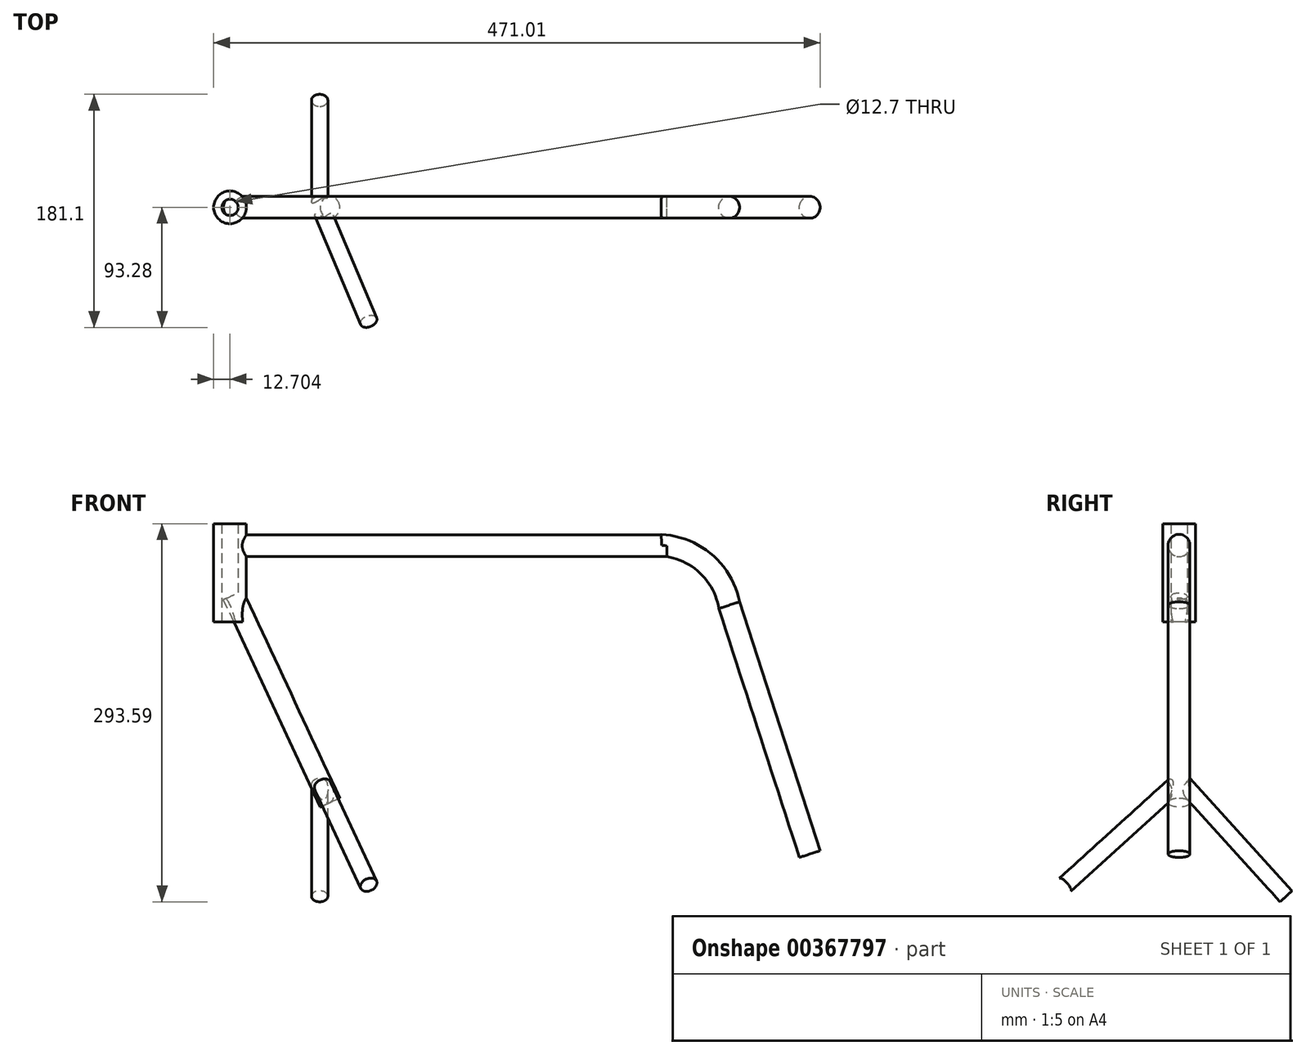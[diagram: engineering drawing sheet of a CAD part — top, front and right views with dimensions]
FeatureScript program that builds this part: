
annotation { "Feature Type Name" : "Feature", "Feature Type Description" : "" }
export const myFeature = defineFeature(function(context is Context, id is Id, definition is map)
    precondition{}
    {
        {
            var Q0;
            Q0=qCreatedBy(makeId("Top.planeOp"),FACE);
            var sketch = newSketch(context, id + "F0", { "sketchPlane" : qUnion([Q0])});
            skCircle(sketch, "E0", {"center": v(-127.53, 0) * mm, "radius": 12.7 * mm});
            skSolve(sketch);
        }
        {
            var Q0;
            Q0 = qSketchRegion(id + "F0", true);
            extrude(context, id + "F1", {"entities" : qUnion([Q0]), "depth" : 76.2 * mm});
        }
        {
            var Q0;
            Q0=makeQuery(id+"F1.opExtrude","CAP_FACE",FACE,{"disambiguationData":[OSD([sQuery(id+"F0.wireOp",EDGE,"E0")])],"isStart":false});
            var sketch = newSketch(context, id + "F2", { "sketchPlane" : qUnion([Q0])});
            skPoint(sketch, "E1", {"position": v(-127.53, 0) * mm});
            skSolve(sketch);
        }
        {
            var Q0;
            Q0=makeQuery(id+"F1.opExtrude","CAP_FACE",FACE,{"disambiguationData":[OSD([sQuery(id+"F0.wireOp",EDGE,"E0")])],"isStart":true});
            var sketch = newSketch(context, id + "F3", { "sketchPlane" : qUnion([Q0])});
            skPoint(sketch, "E2", {"position": v(-127.53, 0) * mm});
            skSolve(sketch);
        }
        {
            var Q0;
            Q0=sQuery(id+"F3.wireOp",VERTEX,"E2");
            var Q1;
            Q1=sQuery(id+"F2.wireOp",VERTEX,"E1");
            var Q2;
            Q2=makeQuery(id+"F1.opExtrude","SWEPT_BODY",BODY,{"disambiguationData":[OSD([sQuery(id+"F0.wireOp",EDGE,"E0")])]});
            hole(context, id + "F4", {"style" : HoleStyle.SIMPLE, "endStyle" : HoleEndStyle.THROUGH, "holeDiameter" : 12.7 * mm, "isTappedThrough" : true, "tappedDepth" : 12.7 * mm, "tapClearance" : 3, "locations" : qUnion([Q0, Q1]), "scope" : qUnion([Q2])});
        }
        {
            var Q0;
            Q0=qCreatedBy(makeId("Right.planeOp"),FACE);
            cPlane(context, id + "F5", {"entities" : qUnion([Q0]), "cplaneType" : CPlaneType.OFFSET, "offset" : 118.49 * mm, "oppositeDirection" : true, "width" : 152.4 * mm, "height" : 152.4 * mm});
        }
        {
            var Q0;
            Q0=qCreatedBy(id+"F5.planeOp",FACE);
            var sketch = newSketch(context, id + "F6", { "sketchPlane" : qUnion([Q0])});
            skCircle(sketch, "E3", {"center": v(0, 59.12) * mm, "radius": 8.47 * mm});
            skSolve(sketch);
        }
        {
            var Q0;
            Q0 = qSketchRegion(id + "F6", true);
            extrude(context, id + "F7", {"entities" : qUnion([Q0]), "operationType" : NewBodyOperationType.ADD, "depth" : 330.2 * mm});
        }
        {
            var Q0;
            Q0=qCreatedBy(id+"F5.planeOp",FACE);
            var sketch = newSketch(context, id + "F8", { "sketchPlane" : qUnion([Q0])});
            skLineSegment(sketch, "E4", {"start": v(0, 23.85) * mm, "end": v(152.27, 23.85) * mm});
            skSolve(sketch);
        }
        {
            var Q0;
            Q0=qCreatedBy(id+"F5.planeOp",FACE);
            var Q1;
            Q1=sQuery(id+"F8.wireOp",EDGE,"E4");
            cPlane(context, id + "F9", {"entities" : qUnion([Q0, Q1]), "cplaneType" : CPlaneType.LINE_ANGLE, "offset" : 25.4 * mm, "angle" : 65 * degree, "width" : 152.4 * mm, "height" : 152.4 * mm});
        }
        {
            var Q0;
            Q0=qCreatedBy(id+"F9.planeOp",FACE);
            var sketch = newSketch(context, id + "F10", { "sketchPlane" : qUnion([Q0])});
            skCircle(sketch, "E5", {"center": v(-104.52, 0) * mm, "radius": 8.38 * mm});
            skSolve(sketch);
        }
        {
            var Q0;
            Q0 = qSketchRegion(id + "F10", true);
            extrude(context, id + "F11", {"entities" : qUnion([Q0]), "operationType" : NewBodyOperationType.ADD, "oppositeDirection" : true, "depth" : 177.8 * mm});
        }
        {
            var Q0;
            Q0=qCreatedBy(id+"F9.planeOp",FACE);
            cPlane(context, id + "F12", {"entities" : qUnion([Q0]), "cplaneType" : CPlaneType.OFFSET, "offset" : 166.54 * mm, "oppositeDirection" : true, "width" : 152.4 * mm, "height" : 152.4 * mm});
        }
        {
            var Q0;
            Q0=qCreatedBy(id+"F12.planeOp",FACE);
            var sketch = newSketch(context, id + "F13", { "sketchPlane" : qUnion([Q0])});
            skLineSegment(sketch, "E6", {"start": v(0, 72.18) * mm, "end": v(-141.83, 72.18) * mm});
            skSolve(sketch);
        }
        {
            var Q0;
            Q0=sQuery(id+"F13.wireOp",EDGE,"E6");
            var Q1;
            Q1=qCreatedBy(id+"F12.planeOp",FACE);
            cPlane(context, id + "F14", {"entities" : qUnion([Q0, Q1]), "cplaneType" : CPlaneType.LINE_ANGLE, "offset" : 25.4 * mm, "angle" : 45 * degree, "width" : 152.4 * mm, "height" : 152.4 * mm});
        }
        {
            var Q0;
            Q0=qCreatedBy(id+"F14.planeOp",FACE);
            cPlane(context, id + "F15", {"entities" : qUnion([Q0]), "cplaneType" : CPlaneType.OFFSET, "offset" : 44.45 * mm, "width" : 152.4 * mm, "height" : 152.4 * mm});
        }
        {
            var Q0;
            Q0=qCreatedBy(id+"F15.planeOp",FACE);
            var sketch = newSketch(context, id + "F16", { "sketchPlane" : qUnion([Q0])});
            skCircle(sketch, "E7", {"center": v(-79.5, -91.84) * mm, "radius": 6.76 * mm});
            skSolve(sketch);
        }
        {
            var Q0;
            Q0 = qSketchRegion(id + "F16", true);
            extrude(context, id + "F17", {"entities" : qUnion([Q0]), "operationType" : NewBodyOperationType.ADD, "depth" : 127 * mm});
        }
        {
            var Q0;
            Q0=qCreatedBy(id+"F15.planeOp",FACE);
            var sketch = newSketch(context, id + "F18", { "sketchPlane" : qUnion([Q0])});
            skLineSegment(sketch, "E8", {"start": v(-115.18, -130.2) * mm, "end": v(54.65, -130.2) * mm});
            skSolve(sketch);
        }
        {
            var Q0;
            Q0=qCreatedBy(id+"F15.planeOp",FACE);
            var Q1;
            Q1=sQuery(id+"F18.wireOp",EDGE,"E8");
            cPlane(context, id + "F19", {"entities" : qUnion([Q0, Q1]), "cplaneType" : CPlaneType.LINE_ANGLE, "offset" : 25.4 * mm, "angle" : 90 * degree, "width" : 152.4 * mm, "height" : 152.4 * mm});
        }
        {
            var Q0;
            Q0=qCreatedBy(id+"F19.planeOp",FACE);
            cPlane(context, id + "F20", {"entities" : qUnion([Q0]), "cplaneType" : CPlaneType.OFFSET, "offset" : 38.5 * mm, "width" : 152.4 * mm, "height" : 152.4 * mm});
        }
        {
            var Q0;
            Q0=qCreatedBy(id+"F20.planeOp",FACE);
            cPlane(context, id + "F21", {"entities" : qUnion([Q0]), "cplaneType" : CPlaneType.OFFSET, "offset" : 4.95 * mm, "width" : 152.4 * mm, "height" : 152.4 * mm});
        }
        {
            var Q0;
            Q0=qCreatedBy(id+"F21.planeOp",FACE);
            var sketch = newSketch(context, id + "F22", { "sketchPlane" : qUnion([Q0])});
            skCircle(sketch, "E9", {"center": v(-59.9, -82.48) * mm, "radius": 7.88 * mm});
            skSolve(sketch);
        }
        {
            var Q0;
            Q0 = qSketchRegion(id + "F22", true);
            var sketch = newSketch(context, id + "F23", { "sketchPlane" : qUnion([Q0])});
            skCircle(sketch, "E10", {"center": v(-57.9, -81.54) * mm, "radius": 6.35 * mm});
            skSolve(sketch);
        }
        {
            var Q0;
            Q0 = qSketchRegion(id + "F23", true);
            extrude(context, id + "F24", {"entities" : qUnion([Q0]), "operationType" : NewBodyOperationType.ADD, "oppositeDirection" : true, "depth" : 127 * mm});
        }
        {
            var Q0;
            Q0=qCreatedBy(makeId("Front.planeOp"),FACE);
            var sketch = newSketch(context, id + "F25", { "sketchPlane" : qUnion([Q0])});
            skArc(sketch, "E11", {"start": v(207.86, 58.98) * mm, "mid": v(241.7, 44.8) * mm, "end": v(259.63, 12.82) * mm});
            skSolve(sketch);
        }
        {
            var Q0;
            Q0=makeQuery(id+"F7.opExtrude","CAP_FACE",FACE,{"disambiguationData":[OSD([sQuery(id+"F6.wireOp",EDGE,"E3")])],"isStart":false});
            var Q1;
            Q1=sQuery(id+"F25.wireOp",EDGE,"E11");
            sweep(context, id + "F26", {"operationType" : NewBodyOperationType.ADD, "profiles" : qUnion([Q0]), "path" : qUnion([Q1])});
        }
        {
            var Q0;
            Q0=makeQuery(id+"F26.opSweep","CAP_FACE",FACE,{"disambiguationData":[OSD([sQuery(id+"F6.wireOp",EDGE,"E3"),sQuery(id+"F25.wireOp",VERTEX,"E11.end")])],"isStart":false});
            extrude(context, id + "F27", {"entities" : qUnion([Q0]), "operationType" : NewBodyOperationType.ADD, "depth" : 203.2 * mm});
        }
    });
